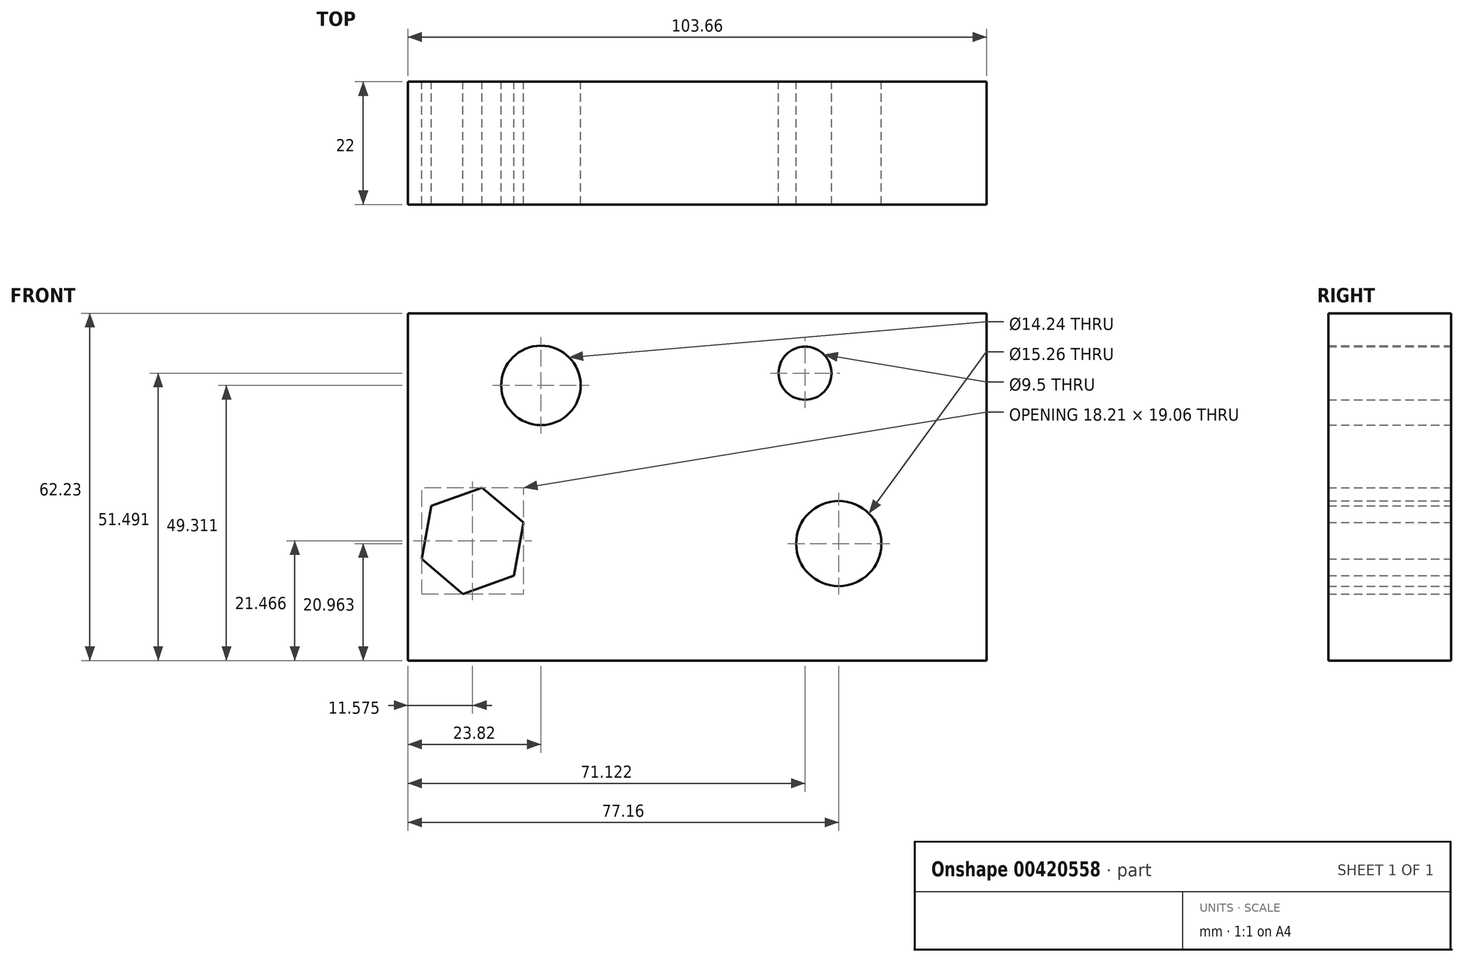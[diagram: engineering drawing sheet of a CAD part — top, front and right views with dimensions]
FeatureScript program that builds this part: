
annotation { "Feature Type Name" : "Feature", "Feature Type Description" : "" }
export const myFeature = defineFeature(function(context is Context, id is Id, definition is map)
    precondition{}
    {
        {
            var Q0;
            Q0=qCreatedBy(makeId("Front.planeOp"),FACE);
            var sketch = newSketch(context, id + "F0", { "sketchPlane" : qUnion([Q0])});
            skLineSegment(sketch, "E0.bottom", {"start": v(-46.8, 23.99) * mm, "end": v(56.86, 23.99) * mm});
            skLineSegment(sketch, "E0.top", {"start": v(-46.8, -38.24) * mm, "end": v(56.86, -38.24) * mm});
            skLineSegment(sketch, "E0.left", {"start": v(-46.8, 23.99) * mm, "end": v(-46.8, -38.24) * mm});
            skLineSegment(sketch, "E0.right", {"start": v(56.86, 23.99) * mm, "end": v(56.86, -38.24) * mm});
            skCircle(sketch, "E1", {"center": v(-22.98, 11.07) * mm, "radius": 7.12 * mm});
            skCircle(sketch, "E2", {"center": v(30.36, -17.28) * mm, "radius": 7.63 * mm});
            skCircle(sketch, "E3", {"center": v(24.32, 13.25) * mm, "radius": 4.75 * mm});
            skCircle(sketch, "E4.cCircle", {"center": v(-35.22, -16.77) * mm, "radius": 8.38 * mm, "construction": true});
            skLineSegment(sketch, "E4.0", {"start": v(-27.82, -23.01) * mm, "end": v(-36.92, -26.3) * mm});
            skLineSegment(sketch, "E4.1", {"start": v(-36.92, -26.3) * mm, "end": v(-44.33, -20.07) * mm});
            skLineSegment(sketch, "E4.2", {"start": v(-44.33, -20.07) * mm, "end": v(-42.63, -10.54) * mm});
            skLineSegment(sketch, "E4.3", {"start": v(-42.63, -10.54) * mm, "end": v(-33.52, -7.24) * mm});
            skLineSegment(sketch, "E4.4", {"start": v(-33.52, -7.24) * mm, "end": v(-26.12, -13.48) * mm});
            skLineSegment(sketch, "E4.5", {"start": v(-26.12, -13.48) * mm, "end": v(-27.82, -23.01) * mm});
            skPoint(sketch, "E4.0.midPoint", {"position": v(-32.37, -24.66) * mm});
            skSolve(sketch);
        }
        {
            var Q0;
            Q0=makeQuery(id+"F0.imprint","IMPRINT",FACE,{"disambiguationData":[TD([[makeQuery(id+"F0.imprint","IMPRINT",EDGE,{"derivedFrom":sQuery(id+"F0.wireOp",EDGE,"E0.bottom")}),-1.0]])]});
            extrude(context, id + "F1", {"entities" : qUnion([Q0]), "depth" : 22 * mm});
        }
    });
